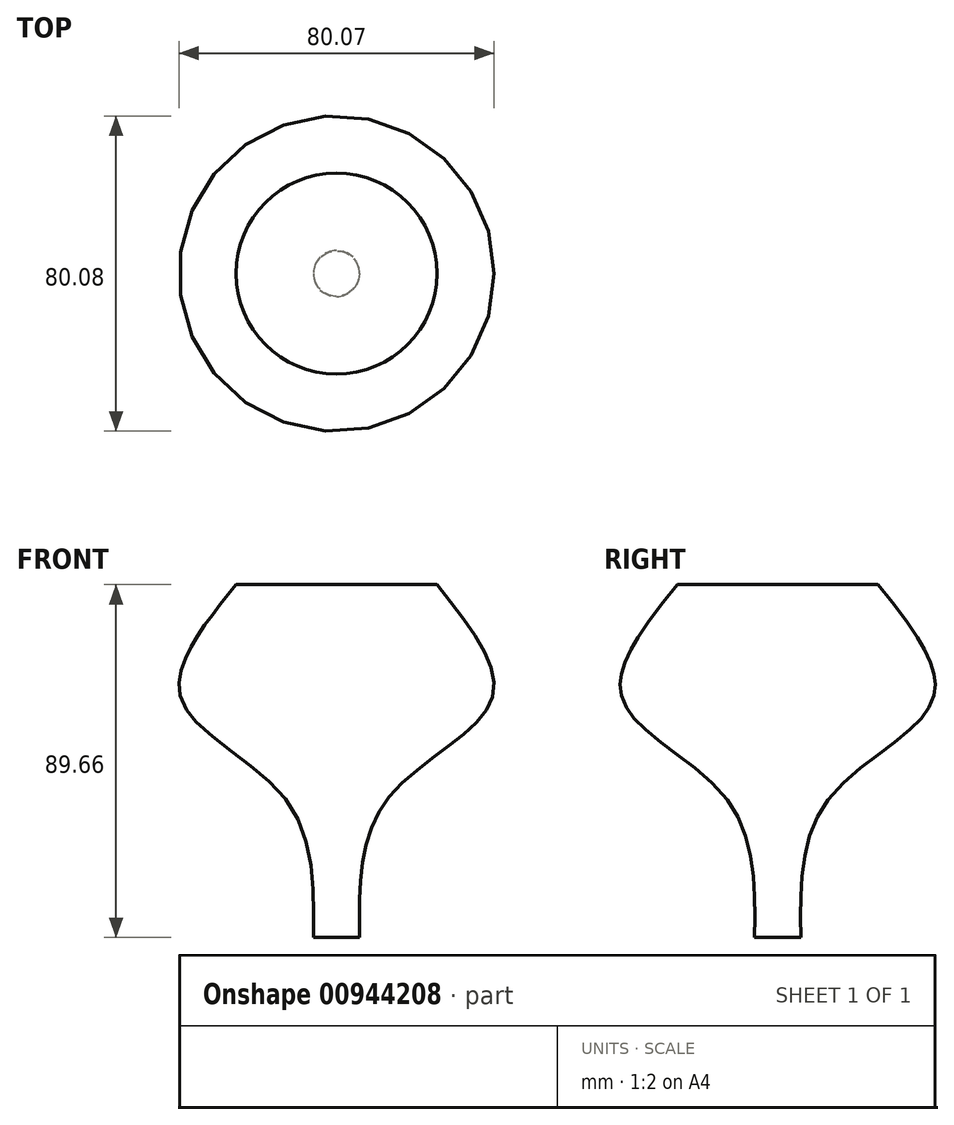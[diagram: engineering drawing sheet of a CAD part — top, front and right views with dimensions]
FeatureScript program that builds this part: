
annotation { "Feature Type Name" : "Feature", "Feature Type Description" : "" }
export const myFeature = defineFeature(function(context is Context, id is Id, definition is map)
    precondition{}
    {
        {
            var Q0;
            Q0=qCreatedBy(makeId("Top.planeOp"),FACE);
            var sketch = newSketch(context, id + "F0", { "sketchPlane" : qUnion([Q0])});
            skCircle(sketch, "E0", {"center": v(0, 0) * mm, "radius": 5.85 * mm});
            skSolve(sketch);
        }
        {
            var Q0;
            Q0=qCreatedBy(makeId("Top.planeOp"),FACE);
            cPlane(context, id + "F1", {"entities" : qUnion([Q0]), "cplaneType" : CPlaneType.OFFSET, "offset" : 89.66 * mm, "width" : 152.4 * mm, "height" : 152.4 * mm});
        }
        {
            var Q0;
            Q0=qCreatedBy(id+"F1.planeOp",FACE);
            var sketch = newSketch(context, id + "F2", { "sketchPlane" : qUnion([Q0])});
            skCircle(sketch, "E1", {"center": v(0, 0) * mm, "radius": 25.52 * mm});
            skSolve(sketch);
        }
        {
            var Q0;
            Q0=qCreatedBy(makeId("Top.planeOp"),FACE);
            cPlane(context, id + "F3", {"entities" : qUnion([Q0]), "cplaneType" : CPlaneType.OFFSET, "offset" : 35.81 * mm, "width" : 152.4 * mm, "height" : 152.4 * mm});
        }
        {
            var Q0;
            Q0=qCreatedBy(makeId("Top.planeOp"),FACE);
            cPlane(context, id + "F4", {"entities" : qUnion([Q0]), "cplaneType" : CPlaneType.OFFSET, "offset" : 61.47 * mm, "width" : 152.4 * mm, "height" : 152.4 * mm});
        }
        {
            var Q0;
            Q0=qCreatedBy(id+"F4.planeOp",FACE);
            var sketch = newSketch(context, id + "F5", { "sketchPlane" : qUnion([Q0])});
            skCircle(sketch, "E2", {"center": v(0, 0) * mm, "radius": 39.73 * mm});
            skSolve(sketch);
        }
        {
            var Q0;
            Q0=qCreatedBy(id+"F3.planeOp",FACE);
            var sketch = newSketch(context, id + "F6", { "sketchPlane" : qUnion([Q0])});
            skCircle(sketch, "E3", {"center": v(0, 0) * mm, "radius": 13.42 * mm});
            skSolve(sketch);
        }
        {
            var Q0;
            Q0=makeQuery(id+"F2.imprint","IMPRINT",FACE,{"disambiguationData":[TD([[makeQuery(id+"F2.imprint","IMPRINT",EDGE,{"derivedFrom":sQuery(id+"F2.wireOp",EDGE,"E1")}),1.0]])]});
            var Q1;
            Q1=makeQuery(id+"F5.imprint","IMPRINT",FACE,{"disambiguationData":[TD([[makeQuery(id+"F5.imprint","IMPRINT",EDGE,{"derivedFrom":sQuery(id+"F5.wireOp",EDGE,"E2")}),1.0]])]});
            var Q2;
            Q2=makeQuery(id+"F6.imprint","IMPRINT",FACE,{"disambiguationData":[TD([[makeQuery(id+"F6.imprint","IMPRINT",EDGE,{"derivedFrom":sQuery(id+"F6.wireOp",EDGE,"E3")}),1.0]])]});
            var Q3;
            Q3=makeQuery(id+"F0.imprint","IMPRINT",FACE,{"disambiguationData":[TD([[makeQuery(id+"F0.imprint","IMPRINT",EDGE,{"derivedFrom":sQuery(id+"F0.wireOp",EDGE,"E0")}),1.0]])]});
            loft(context, id + "F7", {"sheetProfilesArray" : [{ "sheetProfileEntities" : qUnion([Q0]) }, { "sheetProfileEntities" : qUnion([Q1]) }, { "sheetProfileEntities" : qUnion([Q2]) }, { "sheetProfileEntities" : qUnion([Q3]) }]});
        }
    });
